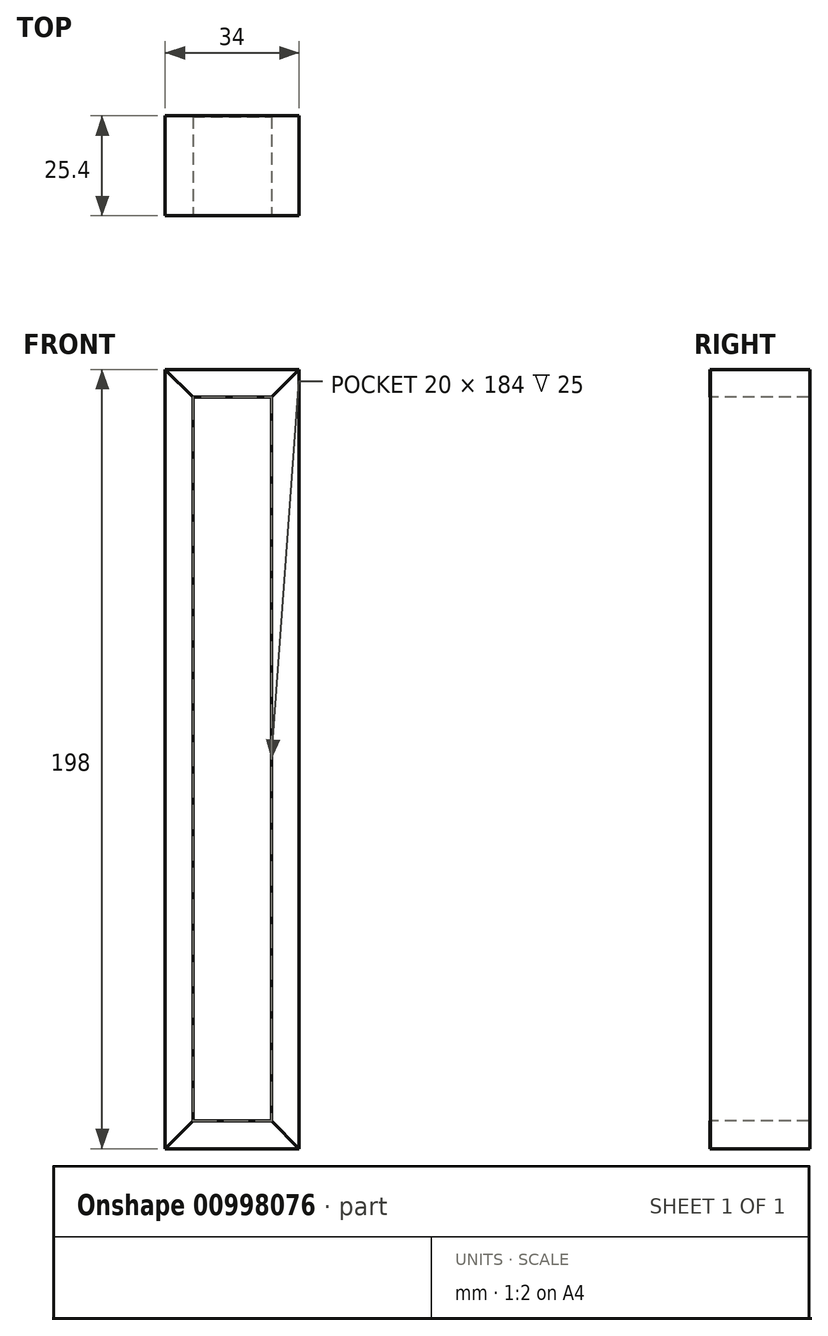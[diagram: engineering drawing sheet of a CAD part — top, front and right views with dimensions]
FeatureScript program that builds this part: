
annotation { "Feature Type Name" : "Feature", "Feature Type Description" : "" }
export const myFeature = defineFeature(function(context is Context, id is Id, definition is map)
    precondition{}
    {
        {
            var Q0;
            Q0=qCreatedBy(makeId("Front.planeOp"),FACE);
            var sketch = newSketch(context, id + "F0", { "sketchPlane" : qUnion([Q0])});
            skLineSegment(sketch, "E0.bottom", {"start": v(17, -99) * mm, "end": v(-17, -99) * mm});
            skLineSegment(sketch, "E0.top", {"start": v(17, 99) * mm, "end": v(-17, 99) * mm});
            skLineSegment(sketch, "E0.left", {"start": v(17, -99) * mm, "end": v(17, 99) * mm});
            skLineSegment(sketch, "E0.right", {"start": v(-17, -99) * mm, "end": v(-17, 99) * mm});
            skPoint(sketch, "E0.middle", {"position": v(0, 0) * mm});
            skSolve(sketch);
        }
        {
            var Q0;
            Q0=makeQuery(id+"F0.imprint","IMPRINT",FACE,{"disambiguationData":[TD([[makeQuery(id+"F0.imprint","IMPRINT",EDGE,{"derivedFrom":sQuery(id+"F0.wireOp",EDGE,"E0.bottom")}),-1.0]])]});
            extrude(context, id + "F1", {"entities" : qUnion([Q0]), "depth" : 25 * mm, "offsetDistance" : 25 * mm});
        }
        {
            var Q0;
            Q0 = qSketchRegion(id + "F0", true);
            extrude(context, id + "F2", {"entities" : qUnion([Q0]), "operationType" : NewBodyOperationType.ADD, "oppositeDirection" : true, "depth" : 0.2 * mm, "offsetDistance" : 25 * mm});
        }
        {
            var Q0;
            Q0=makeQuery(id+"F1.opExtrude","CAP_FACE",FACE,{"disambiguationData":[OSD([sQuery(id+"F0.wireOp",EDGE,"E0.bottom"),sQuery(id+"F0.wireOp",EDGE,"E0.top"),sQuery(id+"F0.wireOp",EDGE,"E0.left"),sQuery(id+"F0.wireOp",EDGE,"E0.right")])],"isStart":false});
            var sketch = newSketch(context, id + "F3", { "sketchPlane" : qUnion([Q0])});
            skLineSegment(sketch, "E1.bottom", {"start": v(-10, 92) * mm, "end": v(10, 92) * mm});
            skLineSegment(sketch, "E1.top", {"start": v(-10, -92) * mm, "end": v(10, -92) * mm});
            skLineSegment(sketch, "E1.left", {"start": v(-10, 92) * mm, "end": v(-10, -92) * mm});
            skLineSegment(sketch, "E1.right", {"start": v(10, 92) * mm, "end": v(10, -92) * mm});
            skPoint(sketch, "E1.middle", {"position": v(0, 0) * mm});
            skSolve(sketch);
        }
        {
            var Q0;
            Q0 = qSketchRegion(id + "F3", true);
            extrude(context, id + "F4", {"entities" : qUnion([Q0]), "operationType" : NewBodyOperationType.REMOVE, "oppositeDirection" : true, "depth" : 25 * mm, "offsetDistance" : 25 * mm});
        }
        {
            var Q0;
            Q0=makeQuery(id+"F1.opExtrude","CAP_FACE",FACE,{"disambiguationData":[OSD([sQuery(id+"F0.wireOp",EDGE,"E0.bottom"),sQuery(id+"F0.wireOp",EDGE,"E0.top"),sQuery(id+"F0.wireOp",EDGE,"E0.left"),sQuery(id+"F0.wireOp",EDGE,"E0.right")])],"isStart":false});
            var sketch = newSketch(context, id + "F5", { "sketchPlane" : qUnion([Q0])});
            skLineSegment(sketch, "E2", {"start": v(-17, 99) * mm, "end": v(-10, 92) * mm});
            skLineSegment(sketch, "E3", {"start": v(-10, 92) * mm, "end": v(10, 92) * mm});
            skLineSegment(sketch, "E4", {"start": v(10, 92) * mm, "end": v(17, 99) * mm});
            skLineSegment(sketch, "E5", {"start": v(17, 99) * mm, "end": v(-17, 99) * mm});
            skLineSegment(sketch, "E6", {"start": v(-17, -99) * mm, "end": v(-10, -92) * mm});
            skLineSegment(sketch, "E7", {"start": v(-10, -92) * mm, "end": v(10, -92) * mm});
            skLineSegment(sketch, "E8", {"start": v(10, -92) * mm, "end": v(17, -99) * mm});
            skLineSegment(sketch, "E9", {"start": v(17, -99) * mm, "end": v(-17, -99) * mm});
            skSolve(sketch);
        }
        {
            var Q0;
            Q0 = qSketchRegion(id + "F5", true);
            extrude(context, id + "F6", {"entities" : qUnion([Q0]), "operationType" : NewBodyOperationType.ADD, "depth" : 0.2 * mm, "offsetDistance" : 25 * mm});
        }
    });
